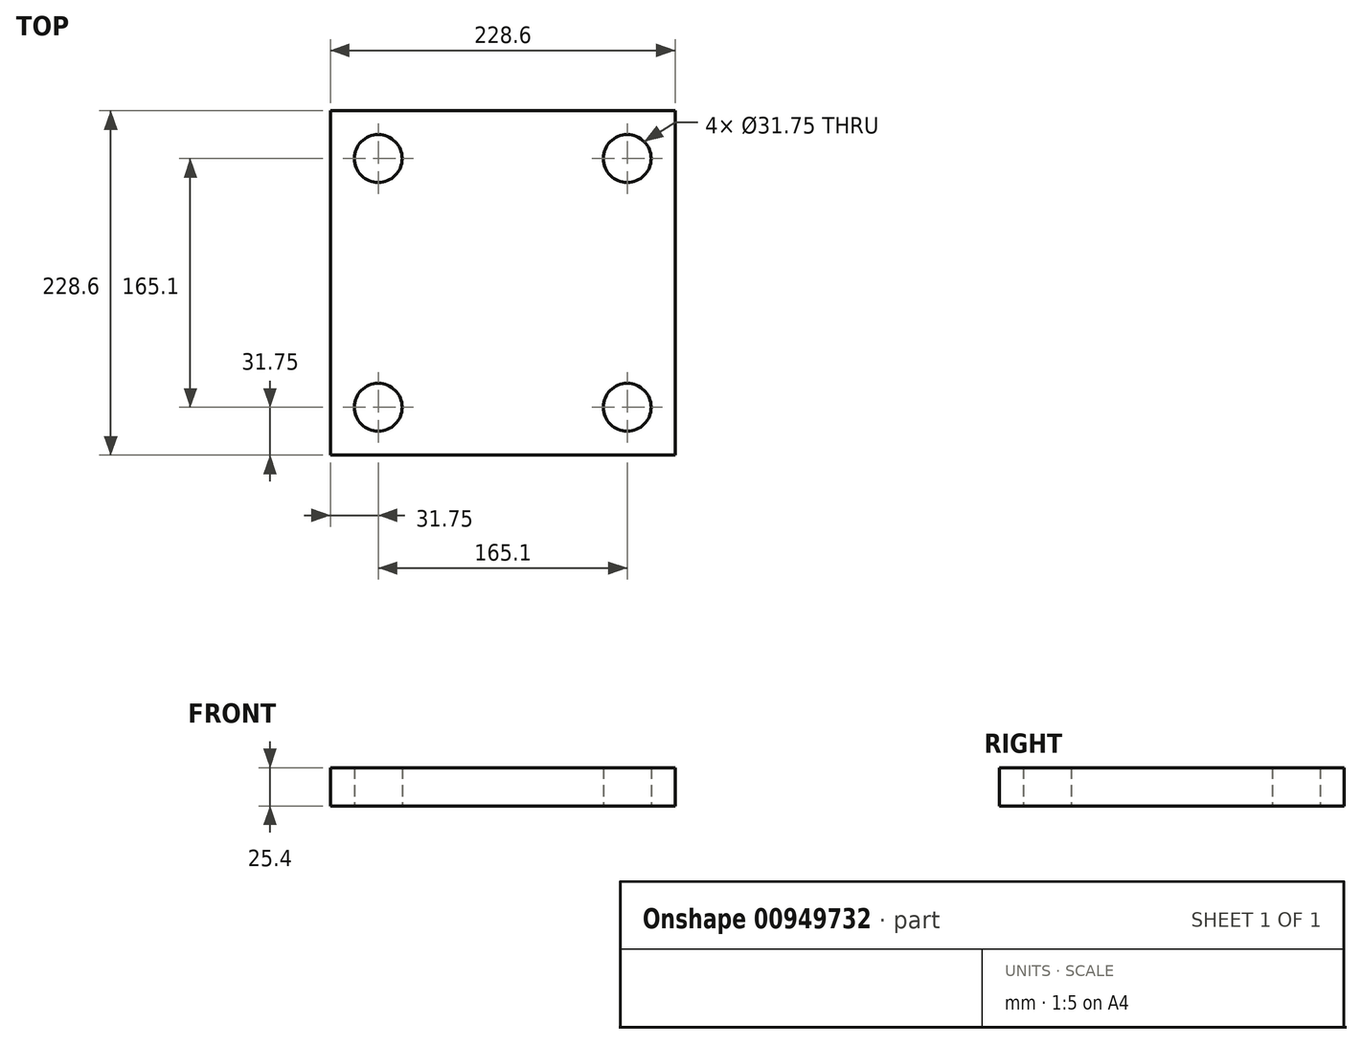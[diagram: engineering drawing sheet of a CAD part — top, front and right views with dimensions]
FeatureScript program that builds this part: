
annotation { "Feature Type Name" : "Feature", "Feature Type Description" : "" }
export const myFeature = defineFeature(function(context is Context, id is Id, definition is map)
    precondition{}
    {
        {
            var Q0;
            Q0=qCreatedBy(makeId("Top.planeOp"),FACE);
            var sketch = newSketch(context, id + "F0", { "sketchPlane" : qUnion([Q0])});
            skLineSegment(sketch, "E0.bottom", {"start": v(-114.3, -114.3) * mm, "end": v(114.3, -114.3) * mm});
            skLineSegment(sketch, "E0.top", {"start": v(-114.3, 114.3) * mm, "end": v(114.3, 114.3) * mm});
            skLineSegment(sketch, "E0.left", {"start": v(-114.3, -114.3) * mm, "end": v(-114.3, 114.3) * mm});
            skLineSegment(sketch, "E0.right", {"start": v(114.3, -114.3) * mm, "end": v(114.3, 114.3) * mm});
            skPoint(sketch, "E0.middle", {"position": v(0, 0) * mm});
            skLineSegment(sketch, "E1.bottom", {"start": v(-82.55, -82.55) * mm, "end": v(82.55, -82.55) * mm, "construction": true});
            skLineSegment(sketch, "E1.top", {"start": v(-82.55, 82.55) * mm, "end": v(82.55, 82.55) * mm, "construction": true});
            skLineSegment(sketch, "E1.left", {"start": v(-82.55, -82.55) * mm, "end": v(-82.55, 82.55) * mm, "construction": true});
            skLineSegment(sketch, "E1.right", {"start": v(82.55, -82.55) * mm, "end": v(82.55, 82.55) * mm, "construction": true});
            skCircle(sketch, "E2", {"center": v(-82.55, 82.55) * mm, "radius": 15.88 * mm});
            skCircle(sketch, "E3", {"center": v(82.55, 82.55) * mm, "radius": 15.88 * mm});
            skCircle(sketch, "E4", {"center": v(82.55, -82.55) * mm, "radius": 15.88 * mm});
            skCircle(sketch, "E5", {"center": v(-82.55, -82.55) * mm, "radius": 15.88 * mm});
            skSolve(sketch);
        }
        {
            var Q0;
            Q0 = qSketchRegion(id + "F0", true);
            extrude(context, id + "F1", {"entities" : qUnion([Q0]), "depth" : 25.4 * mm, "offsetDistance" : 25.4 * mm});
        }
    });
